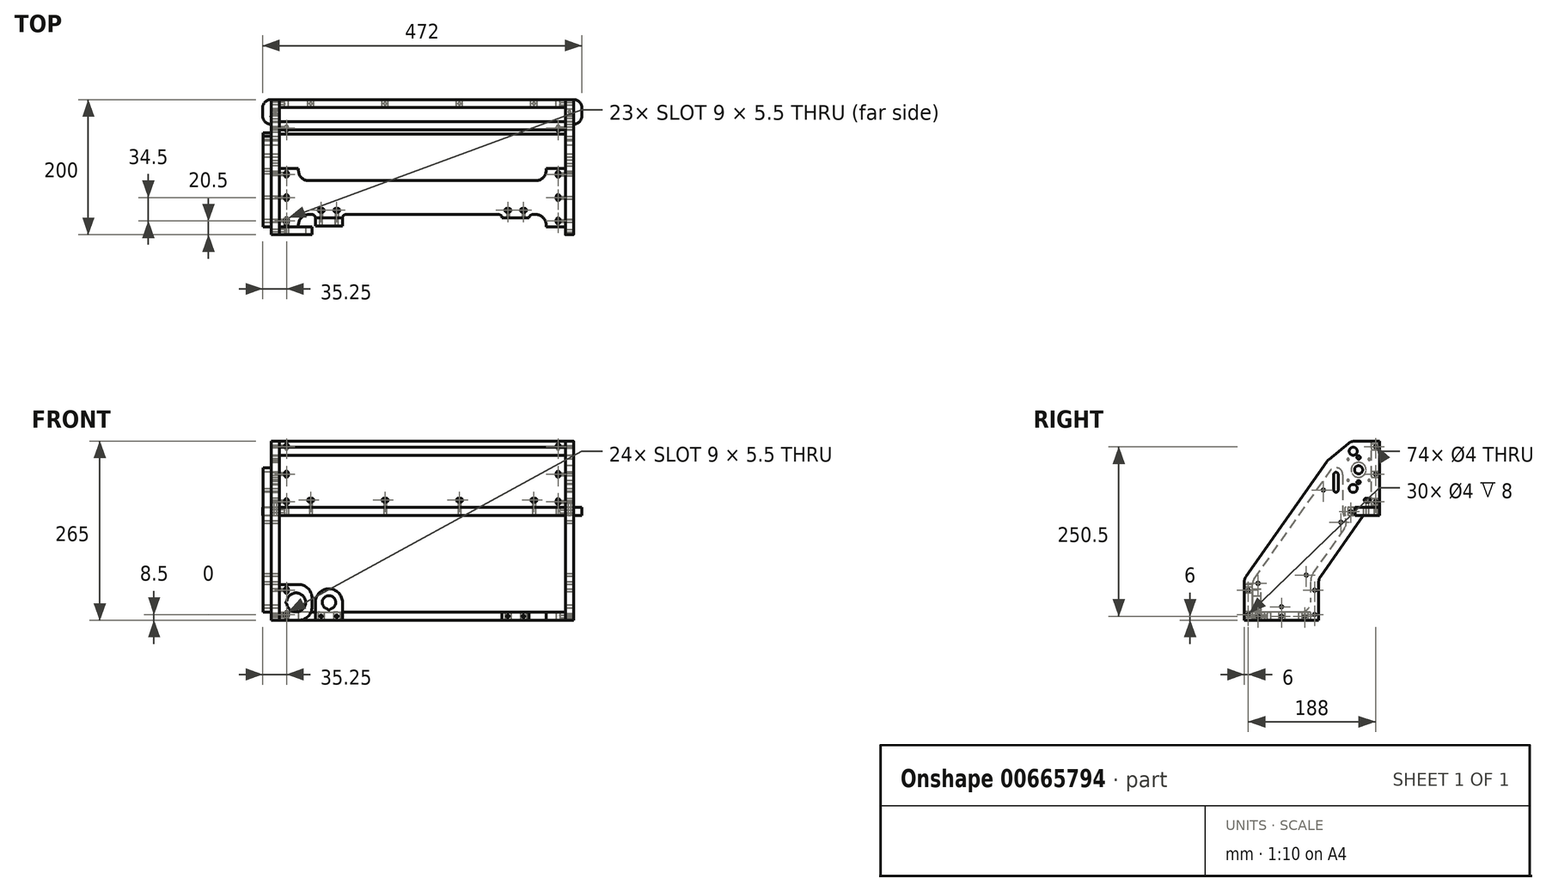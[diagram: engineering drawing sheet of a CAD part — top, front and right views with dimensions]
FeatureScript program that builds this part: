
annotation { "Feature Type Name" : "Feature", "Feature Type Description" : "" }
export const myFeature = defineFeature(function(context is Context, id is Id, definition is map)
    precondition{}
    {
        {
            assignVariable(context, id + "F0", {"name" : "L", "anyValue" : 423});
        }
        {
            var Q0;
            Q0=qCreatedBy(makeId("Front.planeOp"),FACE);
            var sketch = newSketch(context, id + "F1", { "sketchPlane" : qUnion([Q0])});
            skLineSegment(sketch, "E0.bottom", {"start": v(-211.5, 0) * mm, "end": v(211.5, 0) * mm});
            skLineSegment(sketch, "E0.top", {"start": v(-211.5, 98) * mm, "end": v(211.5, 98) * mm});
            skLineSegment(sketch, "E0.left", {"start": v(-211.5, 0) * mm, "end": v(-211.5, 98) * mm});
            skLineSegment(sketch, "E0.right", {"start": v(211.5, 0) * mm, "end": v(211.5, 98) * mm});
            skSolve(sketch);
        }
        {
            var Q0;
            Q0=qSketchRegion(id+"F1",true);
            extrude(context, id + "F2", {"entities" : qUnion([Q0]), "depth" : 12 * mm, "offsetDistance" : 25 * mm});
        }
        {
            var Q0;
            Q0=makeQuery(id+"F2.opExtrude","SWEPT_FACE",FACE,{"disambiguationData":[OSD([sQuery(id+"F1.wireOp",EDGE,"E0.left")])]});
            var sketch = newSketch(context, id + "F3", { "sketchPlane" : qUnion([Q0])});
            skLineSegment(sketch, "E1.bottom", {"start": v(0, 98) * mm, "end": v(56.7, 98) * mm});
            skLineSegment(sketch, "E1.top", {"start": v(90, -167) * mm, "end": v(200, -167) * mm});
            skLineSegment(sketch, "E1.right", {"start": v(56.7, 98) * mm, "end": v(200, -105.92) * mm});
            skLineSegment(sketch, "E2", {"start": v(200, -167) * mm, "end": v(200, -105.92) * mm});
            skLineSegment(sketch, "E3", {"start": v(24, -12) * mm, "end": v(90, -105.92) * mm});
            skLineSegment(sketch, "E4", {"start": v(0, 0) * mm, "end": v(0, 98) * mm});
            skLineSegment(sketch, "E5", {"start": v(90, -167) * mm, "end": v(90, -105.92) * mm});
            skLineSegment(sketch, "E6", {"start": v(0, 0) * mm, "end": v(24, 0) * mm});
            skLineSegment(sketch, "E7", {"start": v(24, 0) * mm, "end": v(24, -12) * mm});
            skSolve(sketch);
        }
        {
            var Q0;
            Q0=qSketchRegion(id+"F3",true);
            extrude(context, id + "F4", {"entities" : qUnion([Q0]), "depth" : 12 * mm, "offsetDistance" : 25 * mm});
        }
        {
            var Q0;
            Q0=makeQuery(id+"F4.opExtrude","CAP_FACE",FACE,{"disambiguationData":[OSD([sQuery(id+"F3.wireOp",EDGE,"E1.bottom"),sQuery(id+"F3.wireOp",EDGE,"E1.top"),sQuery(id+"F3.wireOp",EDGE,"E1.left"),sQuery(id+"F3.wireOp",EDGE,"E1.right"),sQuery(id+"F3.wireOp",EDGE,"E2"),sQuery(id+"F3.wireOp",EDGE,"2146645f-f5f1-4766-9391-dd441536dbd0.filletArc"),sQuery(id+"F3.wireOp",EDGE,"94e26631-0c9e-45e8-bca5-160914bd0a3d.filletArc")])],"isStart":true});
            var sketch = newSketch(context, id + "F5", { "sketchPlane" : qUnion([Q0])});
            skCircle(sketch, "E8", {"center": v(-39, 28) * mm, "radius": 5.97 * mm});
            skCircle(sketch, "E9", {"center": v(-39, 83) * mm, "radius": 5.97 * mm});
            skLineSegment(sketch, "E10", {"start": v(-39, 28) * mm, "end": v(-39, 83) * mm, "construction": true});
            skCircle(sketch, "E11", {"center": v(-31, 55.5) * mm, "radius": 11 * mm});
            skPoint(sketch, "E11.centerSnap0", {"position": v(-39, 55.5) * mm});
            skLineSegment(sketch, "E12.bottom", {"start": v(-15.5, 71) * mm, "end": v(-46.5, 71) * mm, "construction": true});
            skLineSegment(sketch, "E12.top", {"start": v(-15.5, 40) * mm, "end": v(-46.5, 40) * mm, "construction": true});
            skLineSegment(sketch, "E12.left", {"start": v(-15.5, 71) * mm, "end": v(-15.5, 40) * mm, "construction": true});
            skLineSegment(sketch, "E12.right", {"start": v(-46.5, 71) * mm, "end": v(-46.5, 40) * mm, "construction": true});
            skLineSegment(sketch, "E13", {"start": v(-31, 55.5) * mm, "end": v(-31, 71) * mm, "construction": true});
            skLineSegment(sketch, "E14", {"start": v(-15.5, 55.5) * mm, "end": v(-31, 55.5) * mm, "construction": true});
            skCircle(sketch, "E15", {"center": v(-46.5, 71) * mm, "radius": 1.5 * mm});
            skCircle(sketch, "E16.1.0", {"center": v(-46.5, 40) * mm, "radius": 1.5 * mm});
            skCircle(sketch, "E16.2.0", {"center": v(-15.5, 40) * mm, "radius": 1.5 * mm});
            skCircle(sketch, "E16.3.0", {"center": v(-15.5, 71) * mm, "radius": 1.5 * mm});
            skCircle(sketch, "E17", {"center": v(-31, 73.75) * mm, "radius": 2.5 * mm});
            skCircle(sketch, "E18.MirrorC", {"center": v(-31, 37.25) * mm, "radius": 2.5 * mm});
            skSolve(sketch);
        }
        {
            var Q0;
            Q0=qSketchRegion(id+"F5",true);
            extrude(context, id + "F6", {"entities" : qUnion([Q0]), "operationType" : NewBodyOperationType.REMOVE, "oppositeDirection" : true, "depth" : 25 * mm, "offsetDistance" : 25 * mm});
        }
        {
            var Q0;
            Q0=makeQuery(id+"F4.opExtrude","CAP_FACE",FACE,{"disambiguationData":[OSD([sQuery(id+"F3.wireOp",EDGE,"E1.bottom"),sQuery(id+"F3.wireOp",EDGE,"E1.top"),sQuery(id+"F3.wireOp",EDGE,"E1.left"),sQuery(id+"F3.wireOp",EDGE,"E1.right"),sQuery(id+"F3.wireOp",EDGE,"E2"),sQuery(id+"F3.wireOp",EDGE,"2146645f-f5f1-4766-9391-dd441536dbd0.filletArc"),sQuery(id+"F3.wireOp",EDGE,"94e26631-0c9e-45e8-bca5-160914bd0a3d.filletArc")])],"isStart":false});
            var sketch = newSketch(context, id + "F7", { "sketchPlane" : qUnion([Q0])});
            skCircle(sketch, "E19", {"center": v(39, 83) * mm, "radius": 6 * mm});
            skSolve(sketch);
        }
        {
            var Q0;
            Q0=qSketchRegion(id+"F7",true);
            extrude(context, id + "F8", {"entities" : qUnion([Q0]), "oppositeDirection" : true, "depth" : (getVariable(context, 'L') + 24) * mm, "offsetDistance" : 25 * mm});
        }
        {
            var Q0;
            Q0=makeQuery(id+"F2.opExtrude","SWEPT_FACE",FACE,{"disambiguationData":[OSD([sQuery(id+"F1.wireOp",EDGE,"E0.right")])]});
            var sketch = newSketch(context, id + "F9", { "sketchPlane" : qUnion([Q0])});
            skCircle(sketch, "E20.0", {"center": v(-39, 83) * mm, "radius": 5.97 * mm});
            skCircle(sketch, "E21.0", {"center": v(-39, 28) * mm, "radius": 5.97 * mm});
            skLineSegment(sketch, "E22.1", {"start": v(-90, -105.92) * mm, "end": v(-24, -12) * mm});
            skLineSegment(sketch, "E22.5", {"start": v(0, 98) * mm, "end": v(-56.7, 98) * mm});
            skLineSegment(sketch, "E22.6", {"start": v(-56.7, 98) * mm, "end": v(-200, -105.92) * mm});
            skLineSegment(sketch, "E22.8", {"start": v(0, 0) * mm, "end": v(0, 98) * mm});
            skLineSegment(sketch, "E22.9", {"start": v(-200, -105.92) * mm, "end": v(-200, -167) * mm});
            skLineSegment(sketch, "E22.10", {"start": v(-200, -167) * mm, "end": v(-90, -167) * mm});
            skLineSegment(sketch, "E22.11", {"start": v(-90, -167) * mm, "end": v(-90, -105.92) * mm});
            skCircle(sketch, "E23.0", {"center": v(-31, 73.75) * mm, "radius": 2.5 * mm});
            skCircle(sketch, "E24.0", {"center": v(-31, 37.25) * mm, "radius": 2.5 * mm});
            skCircle(sketch, "E25.0", {"center": v(-31, 55.5) * mm, "radius": 6 * mm});
            skLineSegment(sketch, "E26", {"start": v(-24, -12) * mm, "end": v(-24, 0) * mm});
            skLineSegment(sketch, "E27", {"start": v(-24, 0) * mm, "end": v(0, 0) * mm});
            skSolve(sketch);
        }
        {
            var Q0;
            Q0=qSketchRegion(id+"F9",true);
            extrude(context, id + "F10", {"entities" : qUnion([Q0]), "depth" : 12 * mm, "offsetDistance" : 25 * mm});
        }
        {
            var Q0;
            Q0=makeQuery(id+"F4.opExtrude","SWEPT_FACE",FACE,{"disambiguationData":[OSD([sQuery(id+"F3.wireOp",EDGE,"E2")])]});
            var sketch = newSketch(context, id + "F11", { "sketchPlane" : qUnion([Q0])});
            skLineSegment(sketch, "E28.bottom", {"start": v(-211.5, -167) * mm, "end": v(-183, -167) * mm});
            skLineSegment(sketch, "E28.top", {"start": v(-211.5, -114) * mm, "end": v(-183, -114) * mm});
            skLineSegment(sketch, "E28.left", {"start": v(-211.5, -167) * mm, "end": v(-211.5, -114) * mm});
            skLineSegment(sketch, "E28.right", {"start": v(-163, -147) * mm, "end": v(-163, -134) * mm});
            skArc(sketch, "E29", {"start": v(-200.3, -142.7) * mm, "mid": v(-172.52, -140.5) * mm, "end": v(-200.3, -138.3) * mm});
            skPoint(sketch, "E29.centerSnap0", {"position": v(-211.5, -140.5) * mm});
            skPoint(sketch, "E29.centerSnap1", {"position": v(-186.5, -165.5) * mm});
            skArc(sketch, "E30.filletArc", {"start": v(-163, -134) * mm, "mid": v(-168.86, -119.86) * mm, "end": v(-183, -114) * mm});
            skArc(sketch, "E31.filletArc", {"start": v(-183, -167) * mm, "mid": v(-168.86, -161.14) * mm, "end": v(-163, -147) * mm});
            skArc(sketch, "E32", {"start": v(-200.96, -139.08) * mm, "mid": v(-201.97, -140.5) * mm, "end": v(-200.96, -141.92) * mm});
            skPoint(sketch, "E33.visualSharp", {"position": v(-200.4, -139) * mm});
            skArc(sketch, "E33.filletArc", {"start": v(-200.96, -139.08) * mm, "mid": v(-200.52, -138.78) * mm, "end": v(-200.3, -138.3) * mm});
            skPoint(sketch, "E34.visualSharp", {"position": v(-200.4, -142) * mm});
            skArc(sketch, "E34.filletArc", {"start": v(-200.3, -142.7) * mm, "mid": v(-200.52, -142.22) * mm, "end": v(-200.96, -141.92) * mm});
            skSolve(sketch);
        }
        {
            var Q0;
            Q0=qSketchRegion(id+"F11",true);
            extrude(context, id + "F12", {"entities" : qUnion([Q0]), "oppositeDirection" : true, "depth" : 12 * mm, "offsetDistance" : 25 * mm});
        }
        {
            var Q0;
            Q0=makeQuery(id+"F4.opExtrude","SWEPT_FACE",FACE,{"disambiguationData":[OSD([sQuery(id+"F3.wireOp",EDGE,"E1.top")])]});
            var sketch = newSketch(context, id + "F13", { "sketchPlane" : qUnion([Q0])});
            skLineSegment(sketch, "E35.bottom", {"start": v(-168, 170) * mm, "end": v(-163, 170) * mm});
            skLineSegment(sketch, "E35.top", {"start": v(-211.5, 145) * mm, "end": v(211.5, 145) * mm, "construction": true});
            skLineSegment(sketch, "E36.top", {"start": v(-211.5, 188) * mm, "end": v(-183, 188) * mm});
            skPoint(sketch, "E37", {"position": v(-211.5, 145) * mm});
            skLineSegment(sketch, "E38.trimOffspring", {"start": v(-183, 185) * mm, "end": v(-183, 188) * mm});
            skPoint(sketch, "E39.visualSharp", {"position": v(-183, 170) * mm});
            skArc(sketch, "E39.filletArc", {"start": v(-183, 185) * mm, "mid": v(-178.6, 174.4) * mm, "end": v(-168, 170) * mm});
            skLineSegment(sketch, "E40", {"start": v(-211.5, 188) * mm, "end": v(-211.5, 145) * mm});
            skLineSegment(sketch, "E41", {"start": v(0, 145) * mm, "end": v(0, 170) * mm, "construction": true});
            skLineSegment(sketch, "E42.MirrorCS", {"start": v(168, 170) * mm, "end": v(163, 170) * mm});
            skArc(sketch, "E43.MirrorCS", {"start": v(183, 185) * mm, "mid": v(178.6, 174.4) * mm, "end": v(168, 170) * mm});
            skLineSegment(sketch, "E44.MirrorCS", {"start": v(183, 185) * mm, "end": v(183, 188) * mm});
            skLineSegment(sketch, "E45.MirrorCS", {"start": v(211.5, 188) * mm, "end": v(183, 188) * mm});
            skLineSegment(sketch, "E46.MirrorCS", {"start": v(211.5, 188) * mm, "end": v(211.5, 145) * mm});
            skLineSegment(sketch, "E47.MirrorCS", {"start": v(-183, 105) * mm, "end": v(-183, 102) * mm});
            skLineSegment(sketch, "E48.MirrorCS", {"start": v(183, 105) * mm, "end": v(183, 102) * mm});
            skLineSegment(sketch, "E49.MirrorCS", {"start": v(-211.5, 102) * mm, "end": v(-183, 102) * mm});
            skLineSegment(sketch, "E50.MirrorCS", {"start": v(211.5, 102) * mm, "end": v(183, 102) * mm});
            skLineSegment(sketch, "E51.MirrorCS", {"start": v(211.5, 102) * mm, "end": v(211.5, 145) * mm});
            skLineSegment(sketch, "E52.MirrorCS", {"start": v(-168, 120) * mm, "end": v(0, 120) * mm});
            skArc(sketch, "E53.MirrorCS", {"start": v(183, 105) * mm, "mid": v(178.6, 115.6) * mm, "end": v(168, 120) * mm});
            skLineSegment(sketch, "E54.MirrorCS", {"start": v(168, 120) * mm, "end": v(0, 120) * mm});
            skPoint(sketch, "E55.MirrorP", {"position": v(-183, 120) * mm});
            skArc(sketch, "E56.MirrorCS", {"start": v(-183, 105) * mm, "mid": v(-178.6, 115.6) * mm, "end": v(-168, 120) * mm});
            skLineSegment(sketch, "E57.MirrorCS", {"start": v(-211.5, 102) * mm, "end": v(-211.5, 145) * mm});
            skLineSegment(sketch, "E58", {"start": v(-200.75, 108.75) * mm, "end": v(-200.75, 112.25) * mm, "construction": true});
            skArc(sketch, "E59.0.startCap", {"start": v(-198, 108.75) * mm, "mid": v(-200.75, 106) * mm, "end": v(-203.5, 108.75) * mm});
            skArc(sketch, "E59.0.endCap", {"start": v(-203.5, 112.25) * mm, "mid": v(-200.75, 115) * mm, "end": v(-198, 112.25) * mm});
            skLineSegment(sketch, "E59.0.left", {"start": v(-203.5, 108.75) * mm, "end": v(-203.5, 112.25) * mm});
            skLineSegment(sketch, "E59.0.right", {"start": v(-198, 108.75) * mm, "end": v(-198, 112.25) * mm});
            skArc(sketch, "E60.MirrorCS", {"start": v(-203.5, 177.75) * mm, "mid": v(-200.75, 175) * mm, "end": v(-198, 177.75) * mm});
            skLineSegment(sketch, "E61.MirrorCS", {"start": v(-198, 181.25) * mm, "end": v(-198, 177.75) * mm});
            skArc(sketch, "E62.MirrorCS", {"start": v(-203.5, 181.25) * mm, "mid": v(-200.75, 184) * mm, "end": v(-198, 181.25) * mm});
            skLineSegment(sketch, "E63.MirrorCS", {"start": v(-203.5, 181.25) * mm, "end": v(-203.5, 177.75) * mm});
            skLineSegment(sketch, "E64", {"start": v(-200.75, 143.25) * mm, "end": v(-200.75, 146.75) * mm, "construction": true});
            skArc(sketch, "E65.0.startCap", {"start": v(-198, 143.25) * mm, "mid": v(-200.75, 140.5) * mm, "end": v(-203.5, 143.25) * mm});
            skArc(sketch, "E65.0.endCap", {"start": v(-203.5, 146.75) * mm, "mid": v(-200.75, 149.5) * mm, "end": v(-198, 146.75) * mm});
            skLineSegment(sketch, "E65.0.left", {"start": v(-203.5, 143.25) * mm, "end": v(-203.5, 146.75) * mm});
            skLineSegment(sketch, "E65.0.right", {"start": v(-198, 143.25) * mm, "end": v(-198, 146.75) * mm});
            skPoint(sketch, "E66", {"position": v(-200.75, 145) * mm});
            skLineSegment(sketch, "E67.MirrorCS", {"start": v(200.75, 108.75) * mm, "end": v(200.75, 112.25) * mm, "construction": true});
            skLineSegment(sketch, "E68.MirrorCS", {"start": v(200.75, 143.25) * mm, "end": v(200.75, 146.75) * mm, "construction": true});
            skLineSegment(sketch, "E69.MirrorCS", {"start": v(198, 108.75) * mm, "end": v(198, 112.25) * mm});
            skPoint(sketch, "E70.MirrorP", {"position": v(200.75, 145) * mm});
            skLineSegment(sketch, "E71.MirrorCS", {"start": v(203.5, 181.25) * mm, "end": v(203.5, 177.75) * mm});
            skLineSegment(sketch, "E72.MirrorCS", {"start": v(203.5, 143.25) * mm, "end": v(203.5, 146.75) * mm});
            skLineSegment(sketch, "E73.MirrorCS", {"start": v(198, 181.25) * mm, "end": v(198, 177.75) * mm});
            skLineSegment(sketch, "E74.MirrorCS", {"start": v(203.5, 108.75) * mm, "end": v(203.5, 112.25) * mm});
            skLineSegment(sketch, "E75.MirrorCS", {"start": v(198, 143.25) * mm, "end": v(198, 146.75) * mm});
            skArc(sketch, "E76.MirrorCS", {"start": v(203.5, 112.25) * mm, "mid": v(200.75, 115) * mm, "end": v(198, 112.25) * mm});
            skArc(sketch, "E77.MirrorCS", {"start": v(203.5, 181.25) * mm, "mid": v(200.75, 184) * mm, "end": v(198, 181.25) * mm});
            skArc(sketch, "E78.MirrorCS", {"start": v(198, 108.75) * mm, "mid": v(200.75, 106) * mm, "end": v(203.5, 108.75) * mm});
            skArc(sketch, "E79.MirrorCS", {"start": v(203.5, 146.75) * mm, "mid": v(200.75, 149.5) * mm, "end": v(198, 146.75) * mm});
            skPoint(sketch, "E80.MirrorP", {"position": v(183, 120) * mm});
            skArc(sketch, "E81.MirrorCS", {"start": v(203.5, 177.75) * mm, "mid": v(200.75, 175) * mm, "end": v(198, 177.75) * mm});
            skPoint(sketch, "E82.MirrorP", {"position": v(183, 170) * mm});
            skArc(sketch, "E83.MirrorCS", {"start": v(198, 143.25) * mm, "mid": v(200.75, 140.5) * mm, "end": v(203.5, 143.25) * mm});
            skLineSegment(sketch, "E84", {"start": v(-158, 175) * mm, "end": v(-118, 175) * mm});
            skArc(sketch, "E85", {"start": v(-163, 170) * mm, "mid": v(-159.46, 171.46) * mm, "end": v(-158, 175) * mm});
            skPoint(sketch, "E86.orphan", {"position": v(0, 170) * mm});
            skArc(sketch, "E87.MirrorCS", {"start": v(-113, 170) * mm, "mid": v(-116.54, 171.46) * mm, "end": v(-118, 175) * mm});
            skLineSegment(sketch, "E88", {"start": v(-113, 170) * mm, "end": v(0, 170) * mm});
            skLineSegment(sketch, "E89.MirrorCS", {"start": v(113, 170) * mm, "end": v(0, 170) * mm});
            skArc(sketch, "E90.MirrorCS", {"start": v(113, 170) * mm, "mid": v(116.54, 171.46) * mm, "end": v(118, 175) * mm});
            skLineSegment(sketch, "E91.MirrorCS", {"start": v(158, 175) * mm, "end": v(118, 175) * mm});
            skArc(sketch, "E92.MirrorCS", {"start": v(163, 170) * mm, "mid": v(159.46, 171.46) * mm, "end": v(158, 175) * mm});
            skLineSegment(sketch, "E93", {"start": v(-151.25, 163.75) * mm, "end": v(-147.75, 163.75) * mm, "construction": true});
            skArc(sketch, "E94.0.startCap", {"start": v(-151.25, 161) * mm, "mid": v(-154, 163.75) * mm, "end": v(-151.25, 166.5) * mm});
            skArc(sketch, "E94.0.endCap", {"start": v(-147.75, 166.5) * mm, "mid": v(-145, 163.75) * mm, "end": v(-147.75, 161) * mm});
            skLineSegment(sketch, "E94.0.left", {"start": v(-151.25, 166.5) * mm, "end": v(-147.75, 166.5) * mm});
            skLineSegment(sketch, "E94.0.right", {"start": v(-151.25, 161) * mm, "end": v(-147.75, 161) * mm});
            skLineSegment(sketch, "E95", {"start": v(-158, 175) * mm, "end": v(-158, 170) * mm, "construction": true});
            skLineSegment(sketch, "E96", {"start": v(-138, 175) * mm, "end": v(-138, 172.2) * mm, "construction": true});
            skArc(sketch, "E97.MirrorCS", {"start": v(-128.25, 166.5) * mm, "mid": v(-131, 163.75) * mm, "end": v(-128.25, 161) * mm});
            skLineSegment(sketch, "E98.MirrorCS", {"start": v(-124.75, 161) * mm, "end": v(-128.25, 161) * mm});
            skLineSegment(sketch, "E99.MirrorCS", {"start": v(-124.75, 166.5) * mm, "end": v(-128.25, 166.5) * mm});
            skArc(sketch, "E100.MirrorCS", {"start": v(-124.75, 161) * mm, "mid": v(-122, 163.75) * mm, "end": v(-124.75, 166.5) * mm});
            skLineSegment(sketch, "E101.MirrorCS", {"start": v(124.75, 166.5) * mm, "end": v(128.25, 166.5) * mm});
            skLineSegment(sketch, "E102.MirrorCS", {"start": v(151.25, 166.5) * mm, "end": v(147.75, 166.5) * mm});
            skArc(sketch, "E103.MirrorCS", {"start": v(124.75, 161) * mm, "mid": v(122, 163.75) * mm, "end": v(124.75, 166.5) * mm});
            skLineSegment(sketch, "E104.MirrorCS", {"start": v(124.75, 161) * mm, "end": v(128.25, 161) * mm});
            skArc(sketch, "E105.MirrorCS", {"start": v(128.25, 166.5) * mm, "mid": v(131, 163.75) * mm, "end": v(128.25, 161) * mm});
            skArc(sketch, "E106.MirrorCS", {"start": v(147.75, 166.5) * mm, "mid": v(145, 163.75) * mm, "end": v(147.75, 161) * mm});
            skLineSegment(sketch, "E107.MirrorCS", {"start": v(151.25, 161) * mm, "end": v(147.75, 161) * mm});
            skArc(sketch, "E108.MirrorCS", {"start": v(151.25, 161) * mm, "mid": v(154, 163.75) * mm, "end": v(151.25, 166.5) * mm});
            skSolve(sketch);
        }
        {
            var Q0;
            Q0=qSketchRegion(id+"F13",true);
            extrude(context, id + "F14", {"entities" : qUnion([Q0]), "oppositeDirection" : true, "depth" : 12 * mm, "offsetDistance" : 25 * mm});
        }
        {
            var Q0;
            Q0=makeQuery(id+"F12.opExtrude","CAP_FACE",FACE,{"disambiguationData":[OSD([sQuery(id+"F11.wireOp",EDGE,"E28.bottom"),sQuery(id+"F11.wireOp",EDGE,"E28.top"),sQuery(id+"F11.wireOp",EDGE,"E28.left"),sQuery(id+"F11.wireOp",EDGE,"E28.right"),sQuery(id+"F11.wireOp",EDGE,"E29"),sQuery(id+"F11.wireOp",EDGE,"E30.filletArc"),sQuery(id+"F11.wireOp",EDGE,"E31.filletArc")])],"isStart":true});
            var sketch = newSketch(context, id + "F15", { "sketchPlane" : qUnion([Q0])});
            skLineSegment(sketch, "E109", {"start": v(-200.75, -120.75) * mm, "end": v(-200.75, -124.25) * mm, "construction": true});
            skArc(sketch, "E110.0.startCap", {"start": v(-203.5, -120.75) * mm, "mid": v(-200.75, -118) * mm, "end": v(-198, -120.75) * mm});
            skArc(sketch, "E110.0.endCap", {"start": v(-198, -124.25) * mm, "mid": v(-200.75, -127) * mm, "end": v(-203.5, -124.25) * mm});
            skLineSegment(sketch, "E110.0.left", {"start": v(-198, -120.75) * mm, "end": v(-198, -124.25) * mm});
            skLineSegment(sketch, "E110.0.right", {"start": v(-203.5, -120.75) * mm, "end": v(-203.5, -124.25) * mm});
            skLineSegment(sketch, "E111", {"start": v(-211.5, -140.5) * mm, "end": v(-200.47, -140.5) * mm, "construction": true});
            skLineSegment(sketch, "E112.MirrorCS", {"start": v(-198, -160.25) * mm, "end": v(-198, -156.75) * mm});
            skLineSegment(sketch, "E113.MirrorCS", {"start": v(-203.5, -160.25) * mm, "end": v(-203.5, -156.75) * mm});
            skArc(sketch, "E114.MirrorCS", {"start": v(-203.5, -160.25) * mm, "mid": v(-200.75, -163) * mm, "end": v(-198, -160.25) * mm});
            skArc(sketch, "E115.MirrorCS", {"start": v(-198, -156.75) * mm, "mid": v(-200.75, -154) * mm, "end": v(-203.5, -156.75) * mm});
            skSolve(sketch);
        }
        {
            var Q0;
            Q0=qSketchRegion(id+"F15",true);
            extrude(context, id + "F16", {"entities" : qUnion([Q0]), "operationType" : NewBodyOperationType.REMOVE, "oppositeDirection" : true, "depth" : 25 * mm, "offsetDistance" : 25 * mm});
        }
        {
            var Q0;
            Q0=makeQuery(id+"F2.opExtrude","SWEPT_FACE",FACE,{"disambiguationData":[OSD([sQuery(id+"F1.wireOp",EDGE,"E0.bottom")])]});
            var sketch = newSketch(context, id + "F17", { "sketchPlane" : qUnion([Q0])});
            skLineSegment(sketch, "E116", {"start": v(-223.5, 0) * mm, "end": v(223.5, 0) * mm});
            skLineSegment(sketch, "E117", {"start": v(-221.38, 24) * mm, "end": v(-213.62, 24) * mm});
            skLineSegment(sketch, "E118", {"start": v(-211.5, 26.12) * mm, "end": v(-211.5, 51) * mm});
            skLineSegment(sketch, "E119", {"start": v(-211.5, 51) * mm, "end": v(0, 51) * mm});
            skLineSegment(sketch, "E120", {"start": v(0, 51) * mm, "end": v(0, 0) * mm, "construction": true});
            skLineSegment(sketch, "E121.MirrorCS", {"start": v(211.5, 51) * mm, "end": v(0, 51) * mm});
            skLineSegment(sketch, "E122.MirrorCS", {"start": v(211.5, 26.12) * mm, "end": v(211.5, 51) * mm});
            skLineSegment(sketch, "E123.MirrorCS", {"start": v(221.38, 24) * mm, "end": v(213.62, 24) * mm});
            skArc(sketch, "E124", {"start": v(-236, 12.5) * mm, "mid": v(-232.34, 3.66) * mm, "end": v(-223.5, 0) * mm});
            skArc(sketch, "E125", {"start": v(-224.59, 36.45) * mm, "mid": v(-232.72, 32.45) * mm, "end": v(-236, 24) * mm});
            skLineSegment(sketch, "E126", {"start": v(-223.5, 26.12) * mm, "end": v(-223.5, 35.46) * mm});
            skLineSegment(sketch, "E127", {"start": v(-236, 12.5) * mm, "end": v(-236, 24) * mm});
            skPoint(sketch, "E127.startSnap0", {"position": v(-236, 24) * mm});
            skPoint(sketch, "E128.visualSharp", {"position": v(-223.5, 36.5) * mm});
            skArc(sketch, "E128.filletArc", {"start": v(-223.5, 35.46) * mm, "mid": v(-223.82, 36.2) * mm, "end": v(-224.59, 36.45) * mm});
            skArc(sketch, "E129.MirrorCS", {"start": v(223.5, 35.46) * mm, "mid": v(223.82, 36.2) * mm, "end": v(224.59, 36.45) * mm});
            skPoint(sketch, "E130.MirrorP", {"position": v(223.5, 36.5) * mm});
            skLineSegment(sketch, "E131.MirrorCS", {"start": v(236, 12.5) * mm, "end": v(236, 24) * mm});
            skArc(sketch, "E132.MirrorCS", {"start": v(224.59, 36.45) * mm, "mid": v(232.72, 32.45) * mm, "end": v(236, 24) * mm});
            skLineSegment(sketch, "E133.MirrorCS", {"start": v(223.5, 26.12) * mm, "end": v(223.5, 35.46) * mm});
            skPoint(sketch, "E134.MirrorP", {"position": v(236, 24) * mm});
            skArc(sketch, "E135.trimOffspring", {"start": v(236, 12.5) * mm, "mid": v(232.34, 3.66) * mm, "end": v(223.5, 0) * mm});
            skArc(sketch, "E136", {"start": v(-223.5, 26.12) * mm, "mid": v(-223.5, 24) * mm, "end": v(-221.38, 24) * mm});
            skLineSegment(sketch, "E137", {"start": v(-223.5, 26.12) * mm, "end": v(-223.5, 24) * mm, "construction": true});
            skLineSegment(sketch, "E138", {"start": v(-221.38, 24) * mm, "end": v(-223.5, 24) * mm, "construction": true});
            skArc(sketch, "E139.MirrorCS", {"start": v(-211.5, 26.12) * mm, "mid": v(-211.5, 24) * mm, "end": v(-213.62, 24) * mm});
            skArc(sketch, "E140.MirrorCS", {"start": v(223.5, 26.12) * mm, "mid": v(223.5, 24) * mm, "end": v(221.38, 24) * mm});
            skArc(sketch, "E141.MirrorCS", {"start": v(211.5, 26.12) * mm, "mid": v(211.5, 24) * mm, "end": v(213.62, 24) * mm});
            skLineSegment(sketch, "E142", {"start": v(-223.5, 26.12) * mm, "end": v(-211.5, 26.12) * mm, "construction": true});
            skSolve(sketch);
        }
        {
            var Q0;
            Q0=qSketchRegion(id+"F17",true);
            extrude(context, id + "F18", {"entities" : qUnion([Q0]), "depth" : 12 * mm, "offsetDistance" : 25 * mm});
        }
        {
            var Q0;
            Q0=makeQuery(id+"F4.opExtrude","CAP_FACE",FACE,{"disambiguationData":[OSD([sQuery(id+"F3.wireOp",EDGE,"E1.bottom"),sQuery(id+"F3.wireOp",EDGE,"E1.top"),sQuery(id+"F3.wireOp",EDGE,"E1.right"),sQuery(id+"F3.wireOp",EDGE,"E2"),sQuery(id+"F3.wireOp",EDGE,"94e26631-0c9e-45e8-bca5-160914bd0a3d.filletArc"),sQuery(id+"F3.wireOp",EDGE,"E3"),sQuery(id+"F3.wireOp",EDGE,"E4"),sQuery(id+"F3.wireOp",EDGE,"3c304bfc-2885-443d-81d9-234e97ae9333.filletArc"),sQuery(id+"F3.wireOp",EDGE,"E5"),sQuery(id+"F3.wireOp",EDGE,"930fecb7-9af6-459d-8abb-d03ba6c7b7a5.filletArc"),sQuery(id+"F3.wireOp",EDGE,"yWCbbJBZ-1GEx-dhOH-k0kd-LSXJYkVx6NrP"),sQuery(id+"F3.wireOp",EDGE,"cebc93dc-49be-47df-9592-c98bafc6a396.filletArc"),sQuery(id+"F3.wireOp",EDGE,"0R2F742G-mTnw-hJEY-WdgB-tpz7tOERiha1"),sQuery(id+"F3.wireOp",EDGE,"3aeea579-ff88-4944-83f2-f3d4fbf2bd07.filletArc"),sQuery(id+"F3.wireOp",EDGE,"c7c51ab0-1a95-4586-bb57-7b3897809644.filletArc")])],"isStart":false});
            var sketch = newSketch(context, id + "F19", { "sketchPlane" : qUnion([Q0])});
            skCircle(sketch, "E143", {"center": v(194, -158.5) * mm, "radius": 2 * mm});
            skCircle(sketch, "E144", {"center": v(194, -122.5) * mm, "radius": 2 * mm});
            skLineSegment(sketch, "E145", {"start": v(145, -167) * mm, "end": v(145, -142.37) * mm, "construction": true});
            skCircle(sketch, "E146.MirrorC", {"center": v(96, -122.5) * mm, "radius": 2 * mm});
            skCircle(sketch, "E147.MirrorC", {"center": v(96, -158.5) * mm, "radius": 2 * mm});
            skCircle(sketch, "E148", {"center": v(179.5, -161) * mm, "radius": 2 * mm});
            skCircle(sketch, "E149", {"center": v(145, -161) * mm, "radius": 2 * mm});
            skCircle(sketch, "E150.MirrorC", {"center": v(110.5, -161) * mm, "radius": 2 * mm});
            skCircle(sketch, "E151", {"center": v(6, 89.5) * mm, "radius": 2 * mm});
            skCircle(sketch, "E152.0.1.0", {"center": v(6, 49) * mm, "radius": 2 * mm});
            skCircle(sketch, "E152.0.2.0", {"center": v(6, 8.5) * mm, "radius": 2 * mm});
            skLineSegment(sketch, "E152.direction1", {"start": v(6, 89.5) * mm, "end": v(31, 89.5) * mm, "construction": true});
            skLineSegment(sketch, "E152.direction2", {"start": v(6, 89.5) * mm, "end": v(6, 49) * mm, "construction": true});
            skLineSegment(sketch, "E153", {"start": v(16.5, 10.75) * mm, "end": v(20, 10.75) * mm, "construction": true});
            skArc(sketch, "E154.0.startCap", {"start": v(16.5, 8) * mm, "mid": v(13.75, 10.75) * mm, "end": v(16.5, 13.5) * mm});
            skArc(sketch, "E154.0.endCap", {"start": v(20, 13.5) * mm, "mid": v(22.75, 10.75) * mm, "end": v(20, 8) * mm});
            skLineSegment(sketch, "E154.0.left", {"start": v(16.5, 13.5) * mm, "end": v(20, 13.5) * mm});
            skLineSegment(sketch, "E154.0.right", {"start": v(16.5, 8) * mm, "end": v(20, 8) * mm});
            skPoint(sketch, "E155", {"position": v(18.25, 10.75) * mm});
            skCircle(sketch, "E156", {"center": v(42.5, -6) * mm, "radius": 2 * mm});
            skPoint(sketch, "E156.centerSnap0", {"position": v(24, -6) * mm});
            skLineSegment(sketch, "E157", {"start": v(24, -6) * mm, "end": v(51, -6) * mm, "construction": true});
            skSolve(sketch);
        }
        {
            var Q0;
            Q0=qSketchRegion(id+"F19",true);
            extrude(context, id + "F20", {"entities" : qUnion([Q0]), "operationType" : NewBodyOperationType.REMOVE, "oppositeDirection" : true, "depth" : 21 * mm, "offsetDistance" : 25 * mm});
        }
        {
            var Q0;
            Q0=makeQuery(id+"F2.opExtrude","CAP_FACE",FACE,{"disambiguationData":[OSD([sQuery(id+"F1.wireOp",EDGE,"E0.bottom"),sQuery(id+"F1.wireOp",EDGE,"E0.top"),sQuery(id+"F1.wireOp",EDGE,"E0.left"),sQuery(id+"F1.wireOp",EDGE,"E0.right")])],"isStart":true});
            var sketch = newSketch(context, id + "F21", { "sketchPlane" : qUnion([Q0])});
            skLineSegment(sketch, "E158", {"start": v(200.75, 91.25) * mm, "end": v(200.75, 87.75) * mm, "construction": true});
            skArc(sketch, "E159.0.startCap", {"start": v(198, 91.25) * mm, "mid": v(200.75, 94) * mm, "end": v(203.5, 91.25) * mm});
            skArc(sketch, "E159.0.endCap", {"start": v(203.5, 87.75) * mm, "mid": v(200.75, 85) * mm, "end": v(198, 87.75) * mm});
            skLineSegment(sketch, "E159.0.left", {"start": v(203.5, 91.25) * mm, "end": v(203.5, 87.75) * mm});
            skLineSegment(sketch, "E159.0.right", {"start": v(198, 91.25) * mm, "end": v(198, 87.75) * mm});
            skArc(sketch, "E160.0.1.0", {"start": v(198, 50.75) * mm, "mid": v(200.75, 53.5) * mm, "end": v(203.5, 50.75) * mm});
            skLineSegment(sketch, "E160.0.1.1", {"start": v(203.5, 50.75) * mm, "end": v(203.5, 47.25) * mm});
            skArc(sketch, "E160.0.1.2", {"start": v(203.5, 47.25) * mm, "mid": v(200.75, 44.5) * mm, "end": v(198, 47.25) * mm});
            skLineSegment(sketch, "E160.0.1.3", {"start": v(198, 50.75) * mm, "end": v(198, 47.25) * mm});
            skArc(sketch, "E160.0.2.0", {"start": v(198, 10.25) * mm, "mid": v(200.75, 13) * mm, "end": v(203.5, 10.25) * mm});
            skLineSegment(sketch, "E160.0.2.1", {"start": v(203.5, 10.25) * mm, "end": v(203.5, 6.75) * mm});
            skArc(sketch, "E160.0.2.2", {"start": v(203.5, 6.75) * mm, "mid": v(200.75, 4) * mm, "end": v(198, 6.75) * mm});
            skLineSegment(sketch, "E160.0.2.3", {"start": v(198, 10.25) * mm, "end": v(198, 6.75) * mm});
            skLineSegment(sketch, "E160.direction1", {"start": v(159, 87.75) * mm, "end": v(198, 87.75) * mm, "construction": true});
            skLineSegment(sketch, "E160.direction2", {"start": v(198, 87.75) * mm, "end": v(198, 47.25) * mm, "construction": true});
            skLineSegment(sketch, "E161", {"start": v(0, 0) * mm, "end": v(0, 98) * mm, "construction": true});
            skLineSegment(sketch, "E162.MirrorCS", {"start": v(-198, 91.25) * mm, "end": v(-198, 87.75) * mm});
            skLineSegment(sketch, "E163.MirrorCS", {"start": v(-203.5, 91.25) * mm, "end": v(-203.5, 87.75) * mm});
            skLineSegment(sketch, "E164.MirrorCS", {"start": v(-198, 50.75) * mm, "end": v(-198, 47.25) * mm});
            skLineSegment(sketch, "E165.MirrorCS", {"start": v(-203.5, 50.75) * mm, "end": v(-203.5, 47.25) * mm});
            skLineSegment(sketch, "E166.MirrorCS", {"start": v(-203.5, 10.25) * mm, "end": v(-203.5, 6.75) * mm});
            skLineSegment(sketch, "E167.MirrorCS", {"start": v(-198, 10.25) * mm, "end": v(-198, 6.75) * mm});
            skArc(sketch, "E168.MirrorCS", {"start": v(-198, 91.25) * mm, "mid": v(-200.75, 94) * mm, "end": v(-203.5, 91.25) * mm});
            skArc(sketch, "E169.MirrorCS", {"start": v(-203.5, 87.75) * mm, "mid": v(-200.75, 85) * mm, "end": v(-198, 87.75) * mm});
            skArc(sketch, "E170.MirrorCS", {"start": v(-198, 50.75) * mm, "mid": v(-200.75, 53.5) * mm, "end": v(-203.5, 50.75) * mm});
            skArc(sketch, "E171.MirrorCS", {"start": v(-203.5, 47.25) * mm, "mid": v(-200.75, 44.5) * mm, "end": v(-198, 47.25) * mm});
            skArc(sketch, "E172.MirrorCS", {"start": v(-198, 10.25) * mm, "mid": v(-200.75, 13) * mm, "end": v(-203.5, 10.25) * mm});
            skArc(sketch, "E173.MirrorCS", {"start": v(-203.5, 6.75) * mm, "mid": v(-200.75, 4) * mm, "end": v(-198, 6.75) * mm});
            skLineSegment(sketch, "E174", {"start": v(-163.25, 10.75) * mm, "end": v(-166.75, 10.75) * mm, "construction": true});
            skArc(sketch, "E175.0.startCap", {"start": v(-163.25, 13.5) * mm, "mid": v(-160.5, 10.75) * mm, "end": v(-163.25, 8) * mm});
            skArc(sketch, "E175.0.endCap", {"start": v(-166.75, 8) * mm, "mid": v(-169.5, 10.75) * mm, "end": v(-166.75, 13.5) * mm});
            skLineSegment(sketch, "E175.0.left", {"start": v(-163.25, 8) * mm, "end": v(-166.75, 8) * mm});
            skLineSegment(sketch, "E175.0.right", {"start": v(-163.25, 13.5) * mm, "end": v(-166.75, 13.5) * mm});
            skArc(sketch, "E176.1.0.0", {"start": v(-56.75, 8) * mm, "mid": v(-59.5, 10.75) * mm, "end": v(-56.75, 13.5) * mm});
            skLineSegment(sketch, "E176.1.0.1", {"start": v(-53.25, 13.5) * mm, "end": v(-56.75, 13.5) * mm});
            skLineSegment(sketch, "E176.1.0.2", {"start": v(-53.25, 8) * mm, "end": v(-56.75, 8) * mm});
            skArc(sketch, "E176.1.0.3", {"start": v(-53.25, 13.5) * mm, "mid": v(-50.5, 10.75) * mm, "end": v(-53.25, 8) * mm});
            skArc(sketch, "E176.2.0.0", {"start": v(53.25, 8) * mm, "mid": v(50.5, 10.75) * mm, "end": v(53.25, 13.5) * mm});
            skLineSegment(sketch, "E176.2.0.1", {"start": v(56.75, 13.5) * mm, "end": v(53.25, 13.5) * mm});
            skLineSegment(sketch, "E176.2.0.2", {"start": v(56.75, 8) * mm, "end": v(53.25, 8) * mm});
            skArc(sketch, "E176.2.0.3", {"start": v(56.75, 13.5) * mm, "mid": v(59.5, 10.75) * mm, "end": v(56.75, 8) * mm});
            skArc(sketch, "E176.3.0.0", {"start": v(163.25, 8) * mm, "mid": v(160.5, 10.75) * mm, "end": v(163.25, 13.5) * mm});
            skLineSegment(sketch, "E176.3.0.1", {"start": v(166.75, 13.5) * mm, "end": v(163.25, 13.5) * mm});
            skLineSegment(sketch, "E176.3.0.2", {"start": v(166.75, 8) * mm, "end": v(163.25, 8) * mm});
            skArc(sketch, "E176.3.0.3", {"start": v(166.75, 13.5) * mm, "mid": v(169.5, 10.75) * mm, "end": v(166.75, 8) * mm});
            skLineSegment(sketch, "E176.direction1", {"start": v(-166.75, 8) * mm, "end": v(-56.75, 8) * mm, "construction": true});
            skPoint(sketch, "E177", {"position": v(-55, 13.5) * mm});
            skSolve(sketch);
        }
        {
            var Q0;
            Q0=qSketchRegion(id+"F21",true);
            extrude(context, id + "F22", {"entities" : qUnion([Q0]), "operationType" : NewBodyOperationType.REMOVE, "oppositeDirection" : true, "depth" : 25 * mm, "offsetDistance" : 25 * mm});
        }
        {
            var Q0;
            Q0=makeQuery(id+"F10.opExtrude","CAP_FACE",FACE,{"disambiguationData":[OSD([sQuery(id+"F9.wireOp",EDGE,"E20.0"),sQuery(id+"F9.wireOp",EDGE,"E21.0"),sQuery(id+"F9.wireOp",EDGE,"E22.0"),sQuery(id+"F9.wireOp",EDGE,"E22.1"),sQuery(id+"F9.wireOp",EDGE,"E22.2"),sQuery(id+"F9.wireOp",EDGE,"E22.3"),sQuery(id+"F9.wireOp",EDGE,"E22.5"),sQuery(id+"F9.wireOp",EDGE,"E22.6"),sQuery(id+"F9.wireOp",EDGE,"E22.7"),sQuery(id+"F9.wireOp",EDGE,"E22.8"),sQuery(id+"F9.wireOp",EDGE,"E22.9"),sQuery(id+"F9.wireOp",EDGE,"E22.10"),sQuery(id+"F9.wireOp",EDGE,"E22.11"),sQuery(id+"F9.wireOp",EDGE,"E22.12"),sQuery(id+"F9.wireOp",EDGE,"0fa0f1f6-a39c-456d-a7d0-3881c9b7fbf4.0"),sQuery(id+"F9.wireOp",EDGE,"0fa0f1f6-a39c-456d-a7d0-3881c9b7fbf4.2"),sQuery(id+"F9.wireOp",EDGE,"E23.0"),sQuery(id+"F9.wireOp",EDGE,"E24.0"),sQuery(id+"F9.wireOp",EDGE,"E25.0")])],"isStart":false});
            var sketch = newSketch(context, id + "F23", { "sketchPlane" : qUnion([Q0])});
            skCircle(sketch, "E178.0", {"center": v(-96, -122.5) * mm, "radius": 2 * mm});
            skCircle(sketch, "E179.0", {"center": v(-96, -158.5) * mm, "radius": 2 * mm});
            skCircle(sketch, "E180.0", {"center": v(-110.5, -161) * mm, "radius": 2 * mm});
            skCircle(sketch, "E181.0", {"center": v(-145, -161) * mm, "radius": 2 * mm});
            skCircle(sketch, "E182.0", {"center": v(-179.5, -161) * mm, "radius": 2 * mm});
            skCircle(sketch, "E183.0", {"center": v(-194, -158.5) * mm, "radius": 2 * mm});
            skCircle(sketch, "E184.0", {"center": v(-194, -122.5) * mm, "radius": 2 * mm});
            skCircle(sketch, "E185.0", {"center": v(-6, 8.5) * mm, "radius": 2 * mm});
            skCircle(sketch, "E186.0", {"center": v(-6, 49) * mm, "radius": 2 * mm});
            skCircle(sketch, "E187.0", {"center": v(-6, 89.5) * mm, "radius": 2 * mm});
            skCircle(sketch, "E188.0", {"center": v(-42.5, -6) * mm, "radius": 2 * mm});
            skLineSegment(sketch, "E189.0", {"start": v(-16.5, 8) * mm, "end": v(-20, 8) * mm});
            skArc(sketch, "E189.1", {"start": v(-16.5, 8) * mm, "mid": v(-13.75, 10.75) * mm, "end": v(-16.5, 13.5) * mm});
            skLineSegment(sketch, "E189.2", {"start": v(-16.5, 13.5) * mm, "end": v(-20, 13.5) * mm});
            skArc(sketch, "E189.3", {"start": v(-20, 13.5) * mm, "mid": v(-22.75, 10.75) * mm, "end": v(-20, 8) * mm});
            skSolve(sketch);
        }
        {
            var Q0;
            Q0=qSketchRegion(id+"F23",true);
            extrude(context, id + "F24", {"entities" : qUnion([Q0]), "operationType" : NewBodyOperationType.REMOVE, "oppositeDirection" : true, "depth" : 21 * mm, "offsetDistance" : 25 * mm});
        }
        {
            var Q0;
            Q0=makeQuery(id+"F4.opExtrude","SWEPT_EDGE",EDGE,{"disambiguationData":[OSD([sQuery(id+"F3.wireOp",EDGE,"E1.bottom"),sQuery(id+"F3.wireOp",EDGE,"E1.right")])]});
            chamfer(context, id + "F25", {"entities" : qUnion([Q0]), "chamferType" : ChamferType.TWO_OFFSETS, "width1" : 15 * mm, "oppositeDirection" : false, "width2" : 35 * mm, "tangentPropagation" : true});
        }
        {
            var Q0;
            Q0=makeQuery(id+"F10.opExtrude","SWEPT_EDGE",EDGE,{"disambiguationData":[OSD([sQuery(id+"F9.wireOp",EDGE,"E22.5"),sQuery(id+"F9.wireOp",EDGE,"E22.6")])]});
            chamfer(context, id + "F26", {"entities" : qUnion([Q0]), "chamferType" : ChamferType.TWO_OFFSETS, "width1" : 35 * mm, "oppositeDirection" : false, "width2" : 15 * mm, "tangentPropagation" : true});
        }
        {
            var Q0;
            Q0=makeQuery(id+"F4.opExtrude","SWEPT_EDGE",EDGE,{"disambiguationData":[OSD([sQuery(id+"F3.wireOp",EDGE,"E1.right"),sQuery(id+"F3.wireOp",EDGE,"E2")])]});
            var Q1;
            Q1=makeQuery(id+"F10.opExtrude","SWEPT_EDGE",EDGE,{"disambiguationData":[OSD([sQuery(id+"F9.wireOp",EDGE,"E22.6"),sQuery(id+"F9.wireOp",EDGE,"E22.9")])]});
            var Q2;
            Q2=makeQuery(id+"F4.opExtrude","SWEPT_EDGE",EDGE,{"disambiguationData":[OSD([sQuery(id+"F3.wireOp",EDGE,"E3"),sQuery(id+"F3.wireOp",EDGE,"E5")])]});
            var Q3;
            Q3=makeQuery(id+"F10.opExtrude","SWEPT_EDGE",EDGE,{"disambiguationData":[OSD([sQuery(id+"F9.wireOp",EDGE,"E22.1"),sQuery(id+"F9.wireOp",EDGE,"E22.11")])]});
            var Q4;
            {var subQ0=sQuery(id+"F3.wireOp",EDGE,"E1.bottom");Q4=makeQuery(id+"F25.opChamfer","BLEND_EDGE",EDGE,{"blendedFrom":[makeQuery(id+"F4.opExtrude","SWEPT_EDGE",EDGE,{"disambiguationData":[OSD([subQ0,sQuery(id+"F3.wireOp",EDGE,"E1.right")])]}),makeQuery(id+"F4.opExtrude","SWEPT_FACE",FACE,{"disambiguationData":[OSD([subQ0])]})],"blendedInto":[makeQuery(id+"F4.opExtrude","SWEPT_FACE",FACE,{"disambiguationData":[OSD([subQ0])]})]});}
            var Q5;
            {var subQ0=sQuery(id+"F3.wireOp",EDGE,"E1.right");Q5=makeQuery(id+"F25.opChamfer","BLEND_EDGE",EDGE,{"blendedFrom":[makeQuery(id+"F4.opExtrude","SWEPT_EDGE",EDGE,{"disambiguationData":[OSD([sQuery(id+"F3.wireOp",EDGE,"E1.bottom"),subQ0])]}),makeQuery(id+"F4.opExtrude","SWEPT_FACE",FACE,{"disambiguationData":[OSD([subQ0])]})],"blendedInto":[makeQuery(id+"F4.opExtrude","SWEPT_FACE",FACE,{"disambiguationData":[OSD([subQ0])]})]});}
            var Q6;
            {var subQ0=sQuery(id+"F9.wireOp",EDGE,"E22.5");Q6=makeQuery(id+"F26.opChamfer","BLEND_EDGE",EDGE,{"blendedFrom":[makeQuery(id+"F10.opExtrude","SWEPT_EDGE",EDGE,{"disambiguationData":[OSD([subQ0,sQuery(id+"F9.wireOp",EDGE,"E22.6")])]}),makeQuery(id+"F10.opExtrude","SWEPT_FACE",FACE,{"disambiguationData":[OSD([subQ0])]})],"blendedInto":[makeQuery(id+"F10.opExtrude","SWEPT_FACE",FACE,{"disambiguationData":[OSD([subQ0])]})]});}
            var Q7;
            {var subQ0=sQuery(id+"F9.wireOp",EDGE,"E22.6");Q7=makeQuery(id+"F26.opChamfer","BLEND_EDGE",EDGE,{"blendedFrom":[makeQuery(id+"F10.opExtrude","SWEPT_EDGE",EDGE,{"disambiguationData":[OSD([sQuery(id+"F9.wireOp",EDGE,"E22.5"),subQ0])]}),makeQuery(id+"F10.opExtrude","SWEPT_FACE",FACE,{"disambiguationData":[OSD([subQ0])]})],"blendedInto":[makeQuery(id+"F10.opExtrude","SWEPT_FACE",FACE,{"disambiguationData":[OSD([subQ0])]})]});}
            fillet(context, id + "F27", {"entities" : qUnion([Q0, Q1, Q2, Q3, Q4, Q5, Q6, Q7]), "radius" : 15 * mm, "tangentPropagation" : true, "allowEdgeOverflow" : false});
        }
        {
            var Q0;
            Q0=makeQuery(id+"F18.opExtrude","CAP_FACE",FACE,{"disambiguationData":[OSD([sQuery(id+"F17.wireOp",EDGE,"E116"),sQuery(id+"F17.wireOp",EDGE,"cxGHmkkV-L3Ph-Ebet-9txR-TFSqyXeuAXPF"),sQuery(id+"F17.wireOp",EDGE,"E117"),sQuery(id+"F17.wireOp",EDGE,"E118"),sQuery(id+"F17.wireOp",EDGE,"E119"),sQuery(id+"F17.wireOp",EDGE,"3yAaN058-1MfD-fWh8-1EEW-61dTXkiedIJ9"),sQuery(id+"F17.wireOp",EDGE,"fbd00211-0dd4-45b7-a840-197ed4c294e40.MirrorC"),sQuery(id+"F17.wireOp",EDGE,"E121.MirrorCS"),sQuery(id+"F17.wireOp",EDGE,"E122.MirrorCS"),sQuery(id+"F17.wireOp",EDGE,"E123.MirrorCS"),sQuery(id+"F17.wireOp",EDGE,"fbd00211-0dd4-45b7-a840-197ed4c294e44.MirrorCS")])],"isStart":false});
            var sketch = newSketch(context, id + "F28", { "sketchPlane" : qUnion([Q0])});
            skCircle(sketch, "E190", {"center": v(-217.5, 18.25) * mm, "radius": 2 * mm});
            skLineSegment(sketch, "E191", {"start": v(-200.75, 44.25) * mm, "end": v(-200.75, 40.75) * mm, "construction": true});
            skArc(sketch, "E192.0.startCap", {"start": v(-203.5, 44.25) * mm, "mid": v(-200.75, 47) * mm, "end": v(-198, 44.25) * mm});
            skArc(sketch, "E192.0.endCap", {"start": v(-198, 40.75) * mm, "mid": v(-200.75, 38) * mm, "end": v(-203.5, 40.75) * mm});
            skLineSegment(sketch, "E192.0.left", {"start": v(-198, 44.25) * mm, "end": v(-198, 40.75) * mm});
            skLineSegment(sketch, "E192.0.right", {"start": v(-203.5, 44.25) * mm, "end": v(-203.5, 40.75) * mm});
            skLineSegment(sketch, "E193", {"start": v(0, 0) * mm, "end": v(0, 51) * mm, "construction": true});
            skCircle(sketch, "E194.MirrorC", {"center": v(217.5, 18.25) * mm, "radius": 2 * mm});
            skLineSegment(sketch, "E195.MirrorCS", {"start": v(203.5, 44.25) * mm, "end": v(203.5, 40.75) * mm});
            skLineSegment(sketch, "E196.MirrorCS", {"start": v(198, 44.25) * mm, "end": v(198, 40.75) * mm});
            skArc(sketch, "E197.MirrorCS", {"start": v(198, 40.75) * mm, "mid": v(200.75, 38) * mm, "end": v(203.5, 40.75) * mm});
            skArc(sketch, "E198.MirrorCS", {"start": v(203.5, 44.25) * mm, "mid": v(200.75, 47) * mm, "end": v(198, 44.25) * mm});
            skCircle(sketch, "E199", {"center": v(-165, 6) * mm, "radius": 2 * mm});
            skCircle(sketch, "E200.1.0.0", {"center": v(-55, 6) * mm, "radius": 2 * mm});
            skCircle(sketch, "E200.2.0.0", {"center": v(55, 6) * mm, "radius": 2 * mm});
            skCircle(sketch, "E200.3.0.0", {"center": v(165, 6) * mm, "radius": 2 * mm});
            skLineSegment(sketch, "E200.direction1", {"start": v(-165, 6) * mm, "end": v(-55, 6) * mm, "construction": true});
            skSolve(sketch);
        }
        {
            var Q0;
            Q0=qSketchRegion(id+"F28",true);
            extrude(context, id + "F29", {"entities" : qUnion([Q0]), "operationType" : NewBodyOperationType.REMOVE, "oppositeDirection" : true, "depth" : 21 * mm, "offsetDistance" : 25 * mm});
        }
        {
            var Q0;
            Q0=makeQuery(id+"F4.opExtrude","CAP_FACE",FACE,{"disambiguationData":[OSD([sQuery(id+"F3.wireOp",EDGE,"E1.bottom"),sQuery(id+"F3.wireOp",EDGE,"E1.top"),sQuery(id+"F3.wireOp",EDGE,"E1.right"),sQuery(id+"F3.wireOp",EDGE,"E2"),sQuery(id+"F3.wireOp",EDGE,"E3"),sQuery(id+"F3.wireOp",EDGE,"E4"),sQuery(id+"F3.wireOp",EDGE,"E5"),sQuery(id+"F3.wireOp",EDGE,"E6"),sQuery(id+"F3.wireOp",EDGE,"E7")])],"isStart":false});
            var sketch = newSketch(context, id + "F30", { "sketchPlane" : qUnion([Q0])});
            skLineSegment(sketch, "E201.1", {"start": v(188, -155) * mm, "end": v(188, -114.46) * mm});
            skLineSegment(sketch, "E201.2", {"start": v(102, -155) * mm, "end": v(188, -155) * mm});
            skLineSegment(sketch, "E201.10", {"start": v(185.27, -105.83) * mm, "end": v(72.68, 54.39) * mm});
            skLineSegment(sketch, "E201.11", {"start": v(42.88, -18) * mm, "end": v(97.1, -95.14) * mm});
            skArc(sketch, "E201.12", {"start": v(97.1, -95.14) * mm, "mid": v(100.74, -102.52) * mm, "end": v(102, -110.66) * mm});
            skLineSegment(sketch, "E201.13", {"start": v(102, -110.66) * mm, "end": v(102, -155) * mm});
            skArc(sketch, "E202.0", {"start": v(42.88, -18) * mm, "mid": v(51.12, -14.35) * mm, "end": v(54.5, -6) * mm});
            skLineSegment(sketch, "E203", {"start": v(54.5, 48.64) * mm, "end": v(54.5, -6) * mm});
            skArc(sketch, "E204.filletArc", {"start": v(72.68, 54.39) * mm, "mid": v(61.48, 58.17) * mm, "end": v(54.5, 48.64) * mm});
            skArc(sketch, "E205.filletArc", {"start": v(188, -114.46) * mm, "mid": v(187.3, -109.94) * mm, "end": v(185.27, -105.83) * mm});
            skSolve(sketch);
        }
        {
            var Q0;
            Q0=qSketchRegion(id+"F30",true);
            extrude(context, id + "F31", {"entities" : qUnion([Q0]), "depth" : 12 * mm, "offsetDistance" : 25 * mm});
        }
        {
            var Q0;
            Q0=makeQuery(id+"F31.opExtrude","SWEPT_EDGE",EDGE,{"disambiguationData":[OSD([sQuery(id+"F30.wireOp",EDGE,"E201.11"),sQuery(id+"F30.wireOp",EDGE,"E202.0")])]});
            var Q1;
            Q1=makeQuery(id+"F31.opExtrude","SWEPT_EDGE",EDGE,{"disambiguationData":[OSD([sQuery(id+"F30.wireOp",EDGE,"E201.2"),sQuery(id+"F30.wireOp",EDGE,"E201.13")])]});
            var Q2;
            Q2=makeQuery(id+"F31.opExtrude","SWEPT_EDGE",EDGE,{"disambiguationData":[OSD([sQuery(id+"F30.wireOp",EDGE,"E201.1"),sQuery(id+"F30.wireOp",EDGE,"E201.2")])]});
            fillet(context, id + "F32", {"entities" : qUnion([Q0, Q1, Q2]), "radius" : 15 * mm, "tangentPropagation" : true, "allowEdgeOverflow" : false});
        }
        {
            var Q0;
            Q0=makeQuery(id+"F31.opExtrude","CAP_FACE",FACE,{"disambiguationData":[OSD([sQuery(id+"F30.wireOp",EDGE,"E201.1"),sQuery(id+"F30.wireOp",EDGE,"E201.2"),sQuery(id+"F30.wireOp",EDGE,"E201.10"),sQuery(id+"F30.wireOp",EDGE,"E201.11"),sQuery(id+"F30.wireOp",EDGE,"E201.12"),sQuery(id+"F30.wireOp",EDGE,"E201.13"),sQuery(id+"F30.wireOp",EDGE,"E202.0"),sQuery(id+"F30.wireOp",EDGE,"E203"),sQuery(id+"F30.wireOp",EDGE,"E204.filletArc"),sQuery(id+"F30.wireOp",EDGE,"E205.filletArc")])],"isStart":false});
            var sketch = newSketch(context, id + "F33", { "sketchPlane" : qUnion([Q0])});
            skLineSegment(sketch, "E206", {"start": v(64.5, 48.64) * mm, "end": v(64.5, 25.64) * mm, "construction": true});
            skArc(sketch, "E207.0.startCap", {"start": v(61.25, 48.64) * mm, "mid": v(64.5, 51.89) * mm, "end": v(67.75, 48.64) * mm});
            skArc(sketch, "E207.0.endCap", {"start": v(67.75, 25.64) * mm, "mid": v(64.5, 22.39) * mm, "end": v(61.25, 25.64) * mm});
            skLineSegment(sketch, "E207.0.left", {"start": v(67.75, 48.64) * mm, "end": v(67.75, 25.64) * mm});
            skLineSegment(sketch, "E207.0.right", {"start": v(61.25, 48.64) * mm, "end": v(61.25, 25.64) * mm});
            skCircle(sketch, "E208", {"center": v(57.14, -22.05) * mm, "radius": 2 * mm});
            skCircle(sketch, "E209", {"center": v(108.37, -100.11) * mm, "radius": 2 * mm});
            skCircle(sketch, "E210", {"center": v(145, -147) * mm, "radius": 2 * mm});
            skCircle(sketch, "E211", {"center": v(179.67, -112.35) * mm, "radius": 2 * mm});
            skCircle(sketch, "E212", {"center": v(83.1, 25.64) * mm, "radius": 2 * mm});
            skLineSegment(sketch, "E213.0", {"start": v(62.5, 48.64) * mm, "end": v(62.5, -6) * mm, "construction": true});
            skArc(sketch, "E213.1", {"start": v(66.14, 49.79) * mm, "mid": v(63.9, 50.54) * mm, "end": v(62.5, 48.64) * mm, "construction": true});
            skLineSegment(sketch, "E213.2", {"start": v(110, -110.66) * mm, "end": v(110, -140) * mm, "construction": true});
            skArc(sketch, "E213.3", {"start": v(103.64, -90.54) * mm, "mid": v(108.37, -100.11) * mm, "end": v(110, -110.66) * mm, "construction": true});
            skLineSegment(sketch, "E213.4", {"start": v(58.4, -26.18) * mm, "end": v(103.64, -90.54) * mm, "construction": true});
            skArc(sketch, "E213.5", {"start": v(58.53, -17.97) * mm, "mid": v(57.14, -22.05) * mm, "end": v(58.4, -26.18) * mm, "construction": true});
            skArc(sketch, "E213.6", {"start": v(110, -140) * mm, "mid": v(112.05, -144.95) * mm, "end": v(117, -147) * mm, "construction": true});
            skLineSegment(sketch, "E213.7", {"start": v(117, -147) * mm, "end": v(173, -147) * mm, "construction": true});
            skArc(sketch, "E213.8", {"start": v(62.5, -6) * mm, "mid": v(61.48, -12.3) * mm, "end": v(58.53, -17.97) * mm, "construction": true});
            skArc(sketch, "E213.9", {"start": v(173, -147) * mm, "mid": v(177.95, -144.95) * mm, "end": v(180, -140) * mm, "construction": true});
            skLineSegment(sketch, "E213.10", {"start": v(180, -140) * mm, "end": v(180, -114.46) * mm, "construction": true});
            skArc(sketch, "E213.11", {"start": v(180, -114.46) * mm, "mid": v(179.67, -112.35) * mm, "end": v(178.73, -110.43) * mm, "construction": true});
            skLineSegment(sketch, "E213.12", {"start": v(178.73, -110.43) * mm, "end": v(66.14, 49.79) * mm, "construction": true});
            skLineSegment(sketch, "E214", {"start": v(64.5, 25.64) * mm, "end": v(83.1, 25.64) * mm, "construction": true});
            skSolve(sketch);
        }
        {
            var Q0;
            Q0=qSketchRegion(id+"F33",true);
            extrude(context, id + "F34", {"entities" : qUnion([Q0]), "operationType" : NewBodyOperationType.REMOVE, "endBound" : BoundingType.THROUGH_ALL, "oppositeDirection" : true, "depth" : 25 * mm, "offsetDistance" : 25 * mm});
        }
        {
            var Q0;
            Q0=makeQuery(id+"F14.opExtrude","SWEPT_FACE",FACE,{"disambiguationData":[OSD([sQuery(id+"F13.wireOp",EDGE,"E84"),sQuery(id+"F13.wireOp",EDGE,"5ef5005f-9529-4792-9d74-6e6948cf13f80.MirrorCS")])]});
            var sketch = newSketch(context, id + "F35", { "sketchPlane" : qUnion([Q0])});
            skLineSegment(sketch, "E215.left", {"start": v(-158, -167) * mm, "end": v(-158, -140.5) * mm});
            skLineSegment(sketch, "E215.right", {"start": v(-118, -167) * mm, "end": v(-118, -140.5) * mm});
            skPoint(sketch, "E216.visualSharp", {"position": v(-158, -115.02) * mm});
            skCircle(sketch, "E217", {"center": v(-149.5, -161) * mm, "radius": 2 * mm});
            skCircle(sketch, "E218", {"center": v(-126.5, -161) * mm, "radius": 2 * mm});
            skArc(sketch, "E219", {"start": v(-118, -140.5) * mm, "mid": v(-138, -120.5) * mm, "end": v(-158, -140.5) * mm});
            skPoint(sketch, "E219.centerSnap0", {"position": v(-138, -155) * mm});
            skLineSegment(sketch, "E220", {"start": v(-158, -167) * mm, "end": v(-118, -167) * mm});
            skArc(sketch, "E221", {"start": v(-135.83, -150.24) * mm, "mid": v(-138, -130.53) * mm, "end": v(-140.17, -150.24) * mm});
            skArc(sketch, "E222", {"start": v(-139.43, -150.92) * mm, "mid": v(-138, -151.97) * mm, "end": v(-136.57, -150.92) * mm});
            skPoint(sketch, "E223.visualSharp", {"position": v(-139.5, -150.36) * mm});
            skArc(sketch, "E223.filletArc", {"start": v(-139.43, -150.92) * mm, "mid": v(-139.71, -150.48) * mm, "end": v(-140.17, -150.24) * mm});
            skPoint(sketch, "E224.visualSharp", {"position": v(-136.5, -150.36) * mm});
            skArc(sketch, "E224.filletArc", {"start": v(-135.83, -150.24) * mm, "mid": v(-136.29, -150.48) * mm, "end": v(-136.57, -150.92) * mm});
            skSolve(sketch);
        }
        {
            var Q0;
            Q0=qSketchRegion(id+"F35",true);
            extrude(context, id + "F36", {"entities" : qUnion([Q0]), "depth" : 12 * mm, "offsetDistance" : 25 * mm});
        }
        {
            var Q0;
            Q0=makeQuery(id+"F14.opExtrude","SWEPT_FACE",FACE,{"disambiguationData":[OSD([sQuery(id+"F13.wireOp",EDGE,"E91.MirrorCS")])]});
            var sketch = newSketch(context, id + "F37", { "sketchPlane" : qUnion([Q0])});
            skCircle(sketch, "E225.0", {"center": v(-149.5, -161) * mm, "radius": 2 * mm});
            skCircle(sketch, "E226.0", {"center": v(-126.5, -161) * mm, "radius": 2 * mm});
            skLineSegment(sketch, "E227", {"start": v(0, -165.2) * mm, "end": v(0, -155) * mm, "construction": true});
            skCircle(sketch, "E228.MirrorC", {"center": v(149.5, -161) * mm, "radius": 2 * mm});
            skCircle(sketch, "E229.MirrorC", {"center": v(126.5, -161) * mm, "radius": 2 * mm});
            skSolve(sketch);
        }
        {
            var Q0;
            Q0=qSketchRegion(id+"F37",true);
            extrude(context, id + "F38", {"entities" : qUnion([Q0]), "operationType" : NewBodyOperationType.REMOVE, "oppositeDirection" : true, "depth" : 10 * mm, "offsetDistance" : 25 * mm});
        }
        {
            var Q0;
            Q0=makeQuery(id+"F18.opExtrude","SWEPT_EDGE",EDGE,{"disambiguationData":[OSD([sQuery(id+"F17.wireOp",EDGE,"E133.MirrorCS"),sQuery(id+"F17.wireOp",EDGE,"E140.MirrorCS")])]});
            var Q1;
            Q1=makeQuery(id+"F18.opExtrude","SWEPT_EDGE",EDGE,{"disambiguationData":[OSD([sQuery(id+"F17.wireOp",EDGE,"E123.MirrorCS"),sQuery(id+"F17.wireOp",EDGE,"E140.MirrorCS")])]});
            var Q2;
            Q2=makeQuery(id+"F18.opExtrude","SWEPT_EDGE",EDGE,{"disambiguationData":[OSD([sQuery(id+"F17.wireOp",EDGE,"E123.MirrorCS"),sQuery(id+"F17.wireOp",EDGE,"E141.MirrorCS")])]});
            var Q3;
            Q3=makeQuery(id+"F18.opExtrude","SWEPT_EDGE",EDGE,{"disambiguationData":[OSD([sQuery(id+"F17.wireOp",EDGE,"E122.MirrorCS"),sQuery(id+"F17.wireOp",EDGE,"E141.MirrorCS")])]});
            var Q4;
            Q4=makeQuery(id+"F18.opExtrude","SWEPT_EDGE",EDGE,{"disambiguationData":[OSD([sQuery(id+"F17.wireOp",EDGE,"E126"),sQuery(id+"F17.wireOp",EDGE,"E136")])]});
            var Q5;
            Q5=makeQuery(id+"F18.opExtrude","SWEPT_EDGE",EDGE,{"disambiguationData":[OSD([sQuery(id+"F17.wireOp",EDGE,"E117"),sQuery(id+"F17.wireOp",EDGE,"E136")])]});
            var Q6;
            Q6=makeQuery(id+"F18.opExtrude","SWEPT_EDGE",EDGE,{"disambiguationData":[OSD([sQuery(id+"F17.wireOp",EDGE,"E117"),sQuery(id+"F17.wireOp",EDGE,"E139.MirrorCS")])]});
            var Q7;
            Q7=makeQuery(id+"F18.opExtrude","SWEPT_EDGE",EDGE,{"disambiguationData":[OSD([sQuery(id+"F17.wireOp",EDGE,"E118"),sQuery(id+"F17.wireOp",EDGE,"E139.MirrorCS")])]});
            fillet(context, id + "F39", {"entities" : qUnion([Q0, Q1, Q2, Q3, Q4, Q5, Q6, Q7]), "radius" : 1 * mm, "tangentPropagation" : true, "allowEdgeOverflow" : false});
        }
    });
